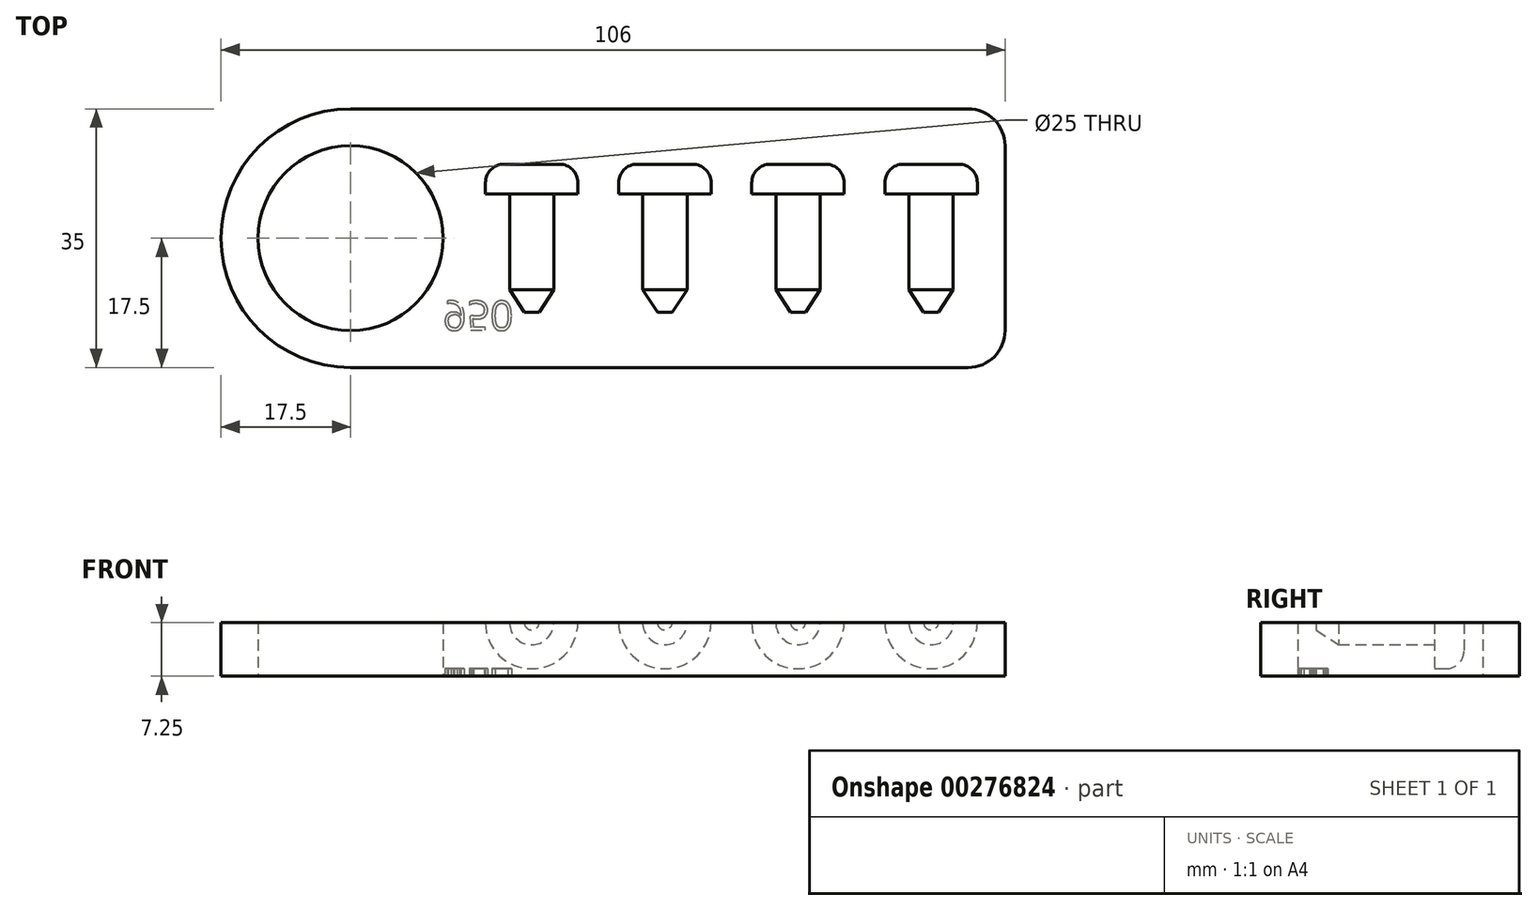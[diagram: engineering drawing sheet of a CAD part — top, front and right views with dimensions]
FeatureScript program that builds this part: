
annotation { "Feature Type Name" : "Feature", "Feature Type Description" : "" }
export const myFeature = defineFeature(function(context is Context, id is Id, definition is map)
    precondition{}
    {
        {
            var Q0;
            Q0=qCreatedBy(makeId("Top.planeOp"),FACE);
            var sketch = newSketch(context, id + "F0", { "sketchPlane" : qUnion([Q0])});
            skLineSegment(sketch, "E0.bottom", {"start": v(17.5, 0) * mm, "end": v(101, 0) * mm});
            skLineSegment(sketch, "E0.top", {"start": v(17.5, 35) * mm, "end": v(101, 35) * mm});
            skLineSegment(sketch, "E0.left", {"start": v(0, 17.5) * mm, "end": v(0, 17.5) * mm});
            skLineSegment(sketch, "E0.right", {"start": v(106, 5) * mm, "end": v(106, 30) * mm});
            skLineSegment(sketch, "E1.bottom", {"start": v(0, 0) * mm, "end": v(17.5, 0) * mm, "construction": true});
            skLineSegment(sketch, "E1.top", {"start": v(0, 17.5) * mm, "end": v(17.5, 17.5) * mm, "construction": true});
            skLineSegment(sketch, "E1.left", {"start": v(0, 0) * mm, "end": v(0, 17.5) * mm, "construction": true});
            skLineSegment(sketch, "E1.right", {"start": v(17.5, 0) * mm, "end": v(17.5, 17.5) * mm, "construction": true});
            skCircle(sketch, "E2", {"center": v(17.5, 17.5) * mm, "radius": 12.5 * mm});
            skPoint(sketch, "E3.visualSharp", {"position": v(0, 0) * mm});
            skArc(sketch, "E3.filletArc", {"start": v(0, 17.5) * mm, "mid": v(5.13, 5.13) * mm, "end": v(17.5, 0) * mm});
            skPoint(sketch, "E4.visualSharp", {"position": v(0, 35) * mm});
            skArc(sketch, "E4.filletArc", {"start": v(17.5, 35) * mm, "mid": v(5.13, 29.87) * mm, "end": v(0, 17.5) * mm});
            skPoint(sketch, "E5.visualSharp", {"position": v(106, 35) * mm});
            skArc(sketch, "E5.filletArc", {"start": v(106, 30) * mm, "mid": v(104.54, 33.54) * mm, "end": v(101, 35) * mm});
            skPoint(sketch, "E6.visualSharp", {"position": v(106, 0) * mm});
            skArc(sketch, "E6.filletArc", {"start": v(101, 0) * mm, "mid": v(104.54, 1.46) * mm, "end": v(106, 5) * mm});
            skSolve(sketch);
        }
        {
            var Q0;
            Q0=makeQuery(id+"F0.imprint","IMPRINT",FACE,{"disambiguationData":[TD([[makeQuery(id+"F0.imprint","IMPRINT",EDGE,{"derivedFrom":sQuery(id+"F0.wireOp",EDGE,"E0.bottom")}),1.0]])]});
            extrude(context, id + "F1", {"entities" : qUnion([Q0]), "depth" : 7.25 * mm});
        }
        {
            var Q0;
            Q0=makeQuery(id+"F1.opExtrude","CAP_FACE",FACE,{"disambiguationData":[OSD([sQuery(id+"F0.wireOp",EDGE,"E0.bottom"),sQuery(id+"F0.wireOp",EDGE,"E0.top"),sQuery(id+"F0.wireOp",EDGE,"E0.right"),sQuery(id+"F0.wireOp",EDGE,"E2"),sQuery(id+"F0.wireOp",EDGE,"E3.filletArc"),sQuery(id+"F0.wireOp",EDGE,"E4.filletArc"),sQuery(id+"F0.wireOp",EDGE,"E5.filletArc"),sQuery(id+"F0.wireOp",EDGE,"E6.filletArc")])],"isStart":false});
            var sketch = newSketch(context, id + "F2", { "sketchPlane" : qUnion([Q0])});
            skLineSegment(sketch, "E7.bottom", {"start": v(0, 0) * mm, "end": v(42, 0) * mm, "construction": true});
            skLineSegment(sketch, "E7.top", {"start": v(0, 7.5) * mm, "end": v(42, 7.5) * mm, "construction": true});
            skLineSegment(sketch, "E7.left", {"start": v(0, 0) * mm, "end": v(0, 7.5) * mm, "construction": true});
            skLineSegment(sketch, "E7.right", {"start": v(42, 0) * mm, "end": v(42, 7.5) * mm, "construction": true});
            skLineSegment(sketch, "E8", {"start": v(42, 7.5) * mm, "end": v(60, 7.5) * mm, "construction": true});
            skLineSegment(sketch, "E9", {"start": v(42, 7.5) * mm, "end": v(42, 23.5) * mm});
            skLineSegment(sketch, "E10", {"start": v(60, 7.5) * mm, "end": v(60, 23.5) * mm});
            skLineSegment(sketch, "E11", {"start": v(60, 7.5) * mm, "end": v(61, 7.5) * mm});
            skLineSegment(sketch, "E12", {"start": v(42, 7.5) * mm, "end": v(43, 7.5) * mm});
            skLineSegment(sketch, "E13.bottom", {"start": v(42, 27.5) * mm, "end": v(45.75, 27.5) * mm});
            skLineSegment(sketch, "E13.top", {"start": v(45, 23.5) * mm, "end": v(48.25, 23.5) * mm});
            skLineSegment(sketch, "E13.left", {"start": v(42, 27.5) * mm, "end": v(42, 23.5) * mm});
            skLineSegment(sketch, "E13.right", {"start": v(48.25, 25) * mm, "end": v(48.25, 23.5) * mm});
            skLineSegment(sketch, "E14.bottom", {"start": v(60, 27.5) * mm, "end": v(63.75, 27.5) * mm});
            skLineSegment(sketch, "E14.top", {"start": v(63, 23.5) * mm, "end": v(66.25, 23.5) * mm});
            skLineSegment(sketch, "E14.left", {"start": v(60, 27.5) * mm, "end": v(60, 23.5) * mm});
            skLineSegment(sketch, "E14.right", {"start": v(66.25, 25) * mm, "end": v(66.25, 23.5) * mm});
            skLineSegment(sketch, "E15.left", {"start": v(42, 23.5) * mm, "end": v(42, 10.5) * mm});
            skLineSegment(sketch, "E15.right", {"start": v(45, 23.5) * mm, "end": v(45, 10.5) * mm});
            skLineSegment(sketch, "E16.left", {"start": v(60, 23.5) * mm, "end": v(60, 10.5) * mm});
            skLineSegment(sketch, "E16.right", {"start": v(63, 23.5) * mm, "end": v(63, 10.5) * mm});
            skLineSegment(sketch, "E17", {"start": v(43, 7.5) * mm, "end": v(45, 10.5) * mm});
            skLineSegment(sketch, "E18", {"start": v(61, 7.5) * mm, "end": v(63, 10.5) * mm});
            skPoint(sketch, "E19.visualSharp", {"position": v(48.25, 27.5) * mm});
            skArc(sketch, "E19.filletArc", {"start": v(48.25, 25) * mm, "mid": v(47.52, 26.77) * mm, "end": v(45.75, 27.5) * mm});
            skPoint(sketch, "E20.visualSharp", {"position": v(66.25, 27.5) * mm});
            skArc(sketch, "E20.filletArc", {"start": v(66.25, 25) * mm, "mid": v(65.52, 26.77) * mm, "end": v(63.75, 27.5) * mm});
            skLineSegment(sketch, "E21", {"start": v(60, 7.5) * mm, "end": v(78, 7.5) * mm, "construction": true});
            skLineSegment(sketch, "E22", {"start": v(78, 7.5) * mm, "end": v(96, 7.5) * mm, "construction": true});
            skLineSegment(sketch, "E23", {"start": v(96, 7.5) * mm, "end": v(97, 7.5) * mm});
            skLineSegment(sketch, "E24", {"start": v(78, 7.5) * mm, "end": v(79, 7.5) * mm});
            skLineSegment(sketch, "E25", {"start": v(78, 7.5) * mm, "end": v(78, 27.5) * mm});
            skLineSegment(sketch, "E26", {"start": v(96, 7.5) * mm, "end": v(96, 23.5) * mm});
            skLineSegment(sketch, "E27.bottom", {"start": v(78, 27.5) * mm, "end": v(81.75, 27.5) * mm});
            skLineSegment(sketch, "E27.top", {"start": v(81, 23.5) * mm, "end": v(84.25, 23.5) * mm});
            skLineSegment(sketch, "E27.right", {"start": v(84.25, 25) * mm, "end": v(84.25, 23.5) * mm});
            skLineSegment(sketch, "E28.bottom", {"start": v(96, 27.5) * mm, "end": v(99.75, 27.5) * mm});
            skLineSegment(sketch, "E28.top", {"start": v(99, 23.5) * mm, "end": v(102.25, 23.5) * mm});
            skLineSegment(sketch, "E28.left", {"start": v(96, 27.5) * mm, "end": v(96, 23.5) * mm});
            skLineSegment(sketch, "E28.right", {"start": v(102.25, 25) * mm, "end": v(102.25, 23.5) * mm});
            skLineSegment(sketch, "E29.left", {"start": v(78, 23.5) * mm, "end": v(78, 10.5) * mm});
            skLineSegment(sketch, "E29.right", {"start": v(81, 23.5) * mm, "end": v(81, 10.5) * mm});
            skLineSegment(sketch, "E30.left", {"start": v(96, 23.5) * mm, "end": v(96, 10.5) * mm});
            skLineSegment(sketch, "E30.right", {"start": v(99, 23.5) * mm, "end": v(99, 10.5) * mm});
            skLineSegment(sketch, "E31", {"start": v(99, 10.5) * mm, "end": v(97, 7.5) * mm});
            skLineSegment(sketch, "E32", {"start": v(81, 10.5) * mm, "end": v(79, 7.5) * mm});
            skPoint(sketch, "E33.visualSharp", {"position": v(84.25, 27.5) * mm});
            skArc(sketch, "E33.filletArc", {"start": v(84.25, 25) * mm, "mid": v(83.52, 26.77) * mm, "end": v(81.75, 27.5) * mm});
            skPoint(sketch, "E34.visualSharp", {"position": v(102.25, 27.5) * mm});
            skArc(sketch, "E34.filletArc", {"start": v(102.25, 25) * mm, "mid": v(101.52, 26.77) * mm, "end": v(99.75, 27.5) * mm});
            skSolve(sketch);
        }
        {
            var Q0;
            Q0=makeQuery(id+"F2.imprint","IMPRINT",FACE,{"disambiguationData":[TD([[makeQuery(id+"F2.imprint","IMPRINT",EDGE,{"derivedFrom":sQuery(id+"F2.wireOp",EDGE,"E9")}),-1.0]])]});
            var Q1;
            Q1=sQuery(id+"F2.wireOp",EDGE,"E9");
            revolve(context, id + "F3", {"operationType" : NewBodyOperationType.REMOVE, "entities" : qUnion([Q0]), "axis" : qUnion([Q1]), "revolveType" : RevolveType.FULL, "oppositeDirection" : true});
        }
        {
            var Q0;
            Q0=makeQuery(id+"F2.imprint","IMPRINT",FACE,{"disambiguationData":[TD([[makeQuery(id+"F2.imprint","IMPRINT",EDGE,{"derivedFrom":sQuery(id+"F2.wireOp",EDGE,"E10")}),-1.0]])]});
            var Q1;
            Q1=sQuery(id+"F2.wireOp",EDGE,"E10");
            revolve(context, id + "F4", {"operationType" : NewBodyOperationType.REMOVE, "entities" : qUnion([Q0]), "axis" : qUnion([Q1]), "revolveType" : RevolveType.FULL, "oppositeDirection" : true});
        }
        {
            var Q0;
            {var subQ2=sQuery(id+"F2.wireOp",EDGE,"E24");Q0=makeQuery(id+"F2.imprint","IMPRINT",FACE,{"disambiguationData":[TD([[makeQuery(id+"F2.imprint","IMPRINT",EDGE,{"derivedFrom":subQ2}),1.0]])]});}
            var Q1;
            Q1=sQuery(id+"F2.wireOp",EDGE,"E29.left");
            revolve(context, id + "F5", {"operationType" : NewBodyOperationType.REMOVE, "entities" : qUnion([Q0]), "axis" : qUnion([Q1]), "revolveType" : RevolveType.FULL, "oppositeDirection" : true});
        }
        {
            var Q0;
            Q0=makeQuery(id+"F2.imprint","IMPRINT",FACE,{"disambiguationData":[TD([[makeQuery(id+"F2.imprint","IMPRINT",EDGE,{"derivedFrom":sQuery(id+"F2.wireOp",EDGE,"E23")}),1.0]])]});
            var Q1;
            Q1=sQuery(id+"F2.wireOp",EDGE,"E26");
            revolve(context, id + "F6", {"operationType" : NewBodyOperationType.REMOVE, "entities" : qUnion([Q0]), "axis" : qUnion([Q1]), "revolveType" : RevolveType.FULL, "oppositeDirection" : true});
        }
        {
            var Q0;
            Q0=makeQuery(id+"F1.opExtrude","CAP_FACE",FACE,{"disambiguationData":[OSD([sQuery(id+"F0.wireOp",EDGE,"E0.bottom"),sQuery(id+"F0.wireOp",EDGE,"E0.top"),sQuery(id+"F0.wireOp",EDGE,"E0.right"),sQuery(id+"F0.wireOp",EDGE,"E2"),sQuery(id+"F0.wireOp",EDGE,"E3.filletArc"),sQuery(id+"F0.wireOp",EDGE,"E4.filletArc"),sQuery(id+"F0.wireOp",EDGE,"E5.filletArc"),sQuery(id+"F0.wireOp",EDGE,"E6.filletArc")])],"isStart":true});
            var sketch = newSketch(context, id + "F7", { "sketchPlane" : qUnion([Q0])});
            skLineSegment(sketch, "E35.bottom", {"start": v(0, 0) * mm, "end": v(30, 0) * mm, "construction": true});
            skLineSegment(sketch, "E35.top", {"start": v(0, -5) * mm, "end": v(30, -5) * mm, "construction": true});
            skLineSegment(sketch, "E35.left", {"start": v(0, 0) * mm, "end": v(0, -5) * mm, "construction": true});
            skLineSegment(sketch, "E35.right", {"start": v(30, 0) * mm, "end": v(30, -5) * mm, "construction": true});
            skText(sketch, "E36", { "text": "950", "fontName": "OpenSans-Regular.ttf"});
            const initialGuessF7  = {"E36": [0.03, -0.009, 1, 0, 0.004]};
            skSetInitialGuess(sketch, initialGuessF7);
            skSolve(sketch);
        }
        {
            var Q0;
            Q0 = qSketchRegion(id + "F7", true);
            extrude(context, id + "F8", {"entities" : qUnion([Q0]), "operationType" : NewBodyOperationType.REMOVE, "oppositeDirection" : true, "depth" : 1 * mm});
        }
    });
